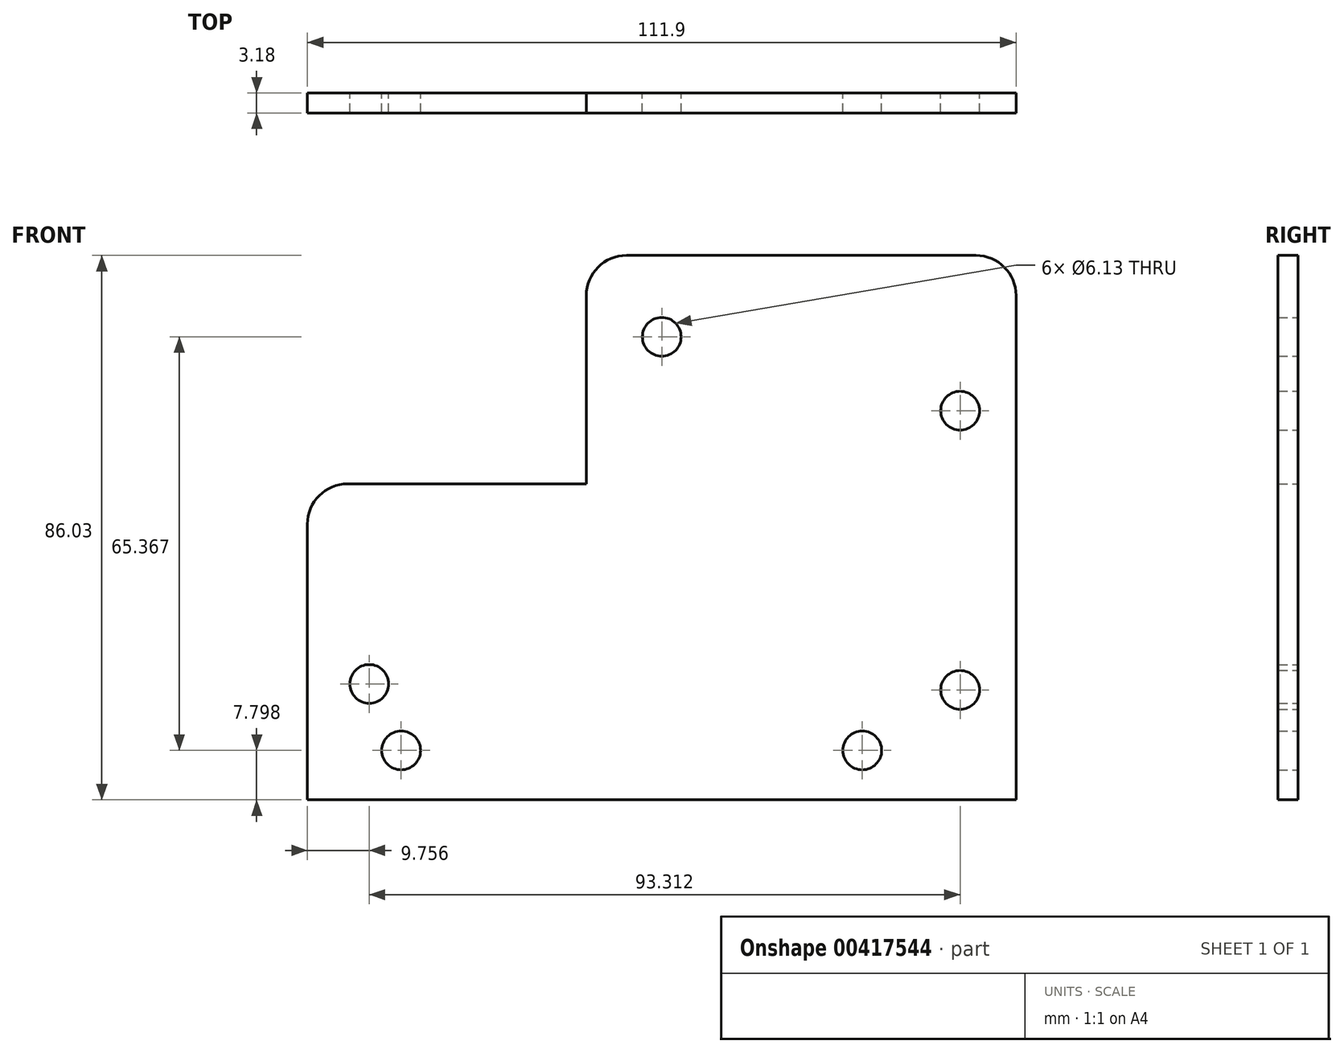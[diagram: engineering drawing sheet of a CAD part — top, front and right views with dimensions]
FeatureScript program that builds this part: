
annotation { "Feature Type Name" : "Feature", "Feature Type Description" : "" }
export const myFeature = defineFeature(function(context is Context, id is Id, definition is map)
    precondition{}
    {
        {
            var Q0;
            Q0=qCreatedBy(makeId("Front.planeOp"),FACE);
            var sketch = newSketch(context, id + "F0", { "sketchPlane" : qUnion([Q0])});
            skLineSegment(sketch, "E0", {"start": v(0, 0) * mm, "end": v(0, 43.58) * mm});
            skLineSegment(sketch, "E1", {"start": v(6.35, 49.93) * mm, "end": v(44.04, 49.93) * mm});
            skLineSegment(sketch, "E2", {"start": v(44.04, 49.93) * mm, "end": v(44.04, 79.68) * mm});
            skLineSegment(sketch, "E3", {"start": v(50.39, 86.03) * mm, "end": v(105.55, 86.03) * mm});
            skLineSegment(sketch, "E4", {"start": v(111.9, 79.68) * mm, "end": v(111.9, 0) * mm});
            skLineSegment(sketch, "E5", {"start": v(111.9, 0) * mm, "end": v(0, 0) * mm});
            skPoint(sketch, "E6.visualSharp", {"position": v(0, 49.93) * mm});
            skArc(sketch, "E6.filletArc", {"start": v(6.35, 49.93) * mm, "mid": v(1.86, 48.07) * mm, "end": v(0, 43.58) * mm});
            skPoint(sketch, "E7.visualSharp", {"position": v(44.04, 86.03) * mm});
            skArc(sketch, "E7.filletArc", {"start": v(50.39, 86.03) * mm, "mid": v(45.9, 84.17) * mm, "end": v(44.04, 79.68) * mm});
            skPoint(sketch, "E8.visualSharp", {"position": v(111.9, 86.03) * mm});
            skArc(sketch, "E8.filletArc", {"start": v(111.9, 79.68) * mm, "mid": v(110.04, 84.17) * mm, "end": v(105.55, 86.03) * mm});
            skLineSegment(sketch, "E9", {"start": v(0, 7.8) * mm, "end": v(111.9, 7.8) * mm, "construction": true});
            skCircle(sketch, "E10", {"center": v(14.8, 7.8) * mm, "radius": 3.06 * mm});
            skCircle(sketch, "E11", {"center": v(87.62, 7.8) * mm, "radius": 3.06 * mm});
            skLineSegment(sketch, "E12", {"start": v(103.07, 0) * mm, "end": v(103.07, 86.03) * mm, "construction": true});
            skCircle(sketch, "E13", {"center": v(103.07, 17.37) * mm, "radius": 3.06 * mm});
            skCircle(sketch, "E14", {"center": v(103.07, 61.5) * mm, "radius": 3.06 * mm});
            skLineSegment(sketch, "E15", {"start": v(55.95, 0) * mm, "end": v(55.95, 86.03) * mm, "construction": true});
            skCircle(sketch, "E16", {"center": v(55.95, 73.16) * mm, "radius": 3.06 * mm});
            skLineSegment(sketch, "E17", {"start": v(0, 35.34) * mm, "end": v(111.9, 35.34) * mm, "construction": true});
            skPoint(sketch, "E17.endSnap0", {"position": v(111.9, 39.84) * mm});
            skLineSegment(sketch, "E18", {"start": v(9.76, 0) * mm, "end": v(9.76, 49.93) * mm, "construction": true});
            skCircle(sketch, "E19", {"center": v(9.76, 18.31) * mm, "radius": 3.06 * mm});
            skSolve(sketch);
        }
        {
            var Q0;
            Q0 = qSketchRegion(id + "F0", true);
            extrude(context, id + "F1", {"entities" : qUnion([Q0]), "depth" : 3.17 * mm});
        }
    });
